# Revit family: 200 SUPER LITE OPENING ROOF
name_source: partatom
category: Generic Models
revit_build: Autodesk Revit 2018 (Build: 20170223_1515(x64)
units: mm (PartAtom-declared; Revit-internal decimal feet)

## family parameters
Always vertical = Yes
Can host rebar = No
Cut with Voids When Loaded = No
Part Type = Normal
Room Calculation Point = No
Round Connector Dimension = Use Diameter
Shared = No
Work Plane-Based = No

## types (1)
- 200 SUPER LITE OPENING ROOF
    185 GUTTER = <By Category>
    200 SUPER LITE BLADE = <By Category>
    200 SUPER LITE END CAP = Steel, Paint Finish, Dark Gray, Matte
    BEAM = <By Category>
    BEAM HEIGHT = 200 mm  [stored 0.656168 ft]
    BEAM THICKNESS = 3 mm  [stored 0.00984252 ft]
    BEAM WIDTH = 50 mm  [stored 0.164042 ft]
    FLASHING = <By Category>
    HEIGHT = 2200 mm  [stored 7.21785 ft]
    LENGTH = 2400 mm  [stored 7.87402 ft]
    LOUVRE ANGLE = 45.00°
    PASSIVE AND DRIVE FRAME = <By Category>
    PITCH = 1.00°
    POST = <By Category>
    POST LENGTH = 100 mm  [stored 0.328084 ft]
    POST THICKNESS = 3 mm  [stored 0.00984252 ft]
    POST WIDTH = 100 mm  [stored 0.328084 ft]
    SPACING = 188 mm  [stored 0.616798 ft]
    VISABLE 185 GUTTER = Yes
    VISABLE 200 SUPER LITE BLADES, AND END CAPS = Yes
    VISABLE BEAM = Yes
    VISABLE FLASHING = Yes
    VISABLE PASSIVE AND DRIVE FRAME = Yes
    VISABLE POST = Yes
    WIDTH = 3164 mm

note: [stored X ft] marks values corroborated as IEEE doubles in the binary element streams (Revit-internal decimal feet)

## geometry (parser evidence)
native form markers: Sweep x34
no freeform markers — native parametric forms only
